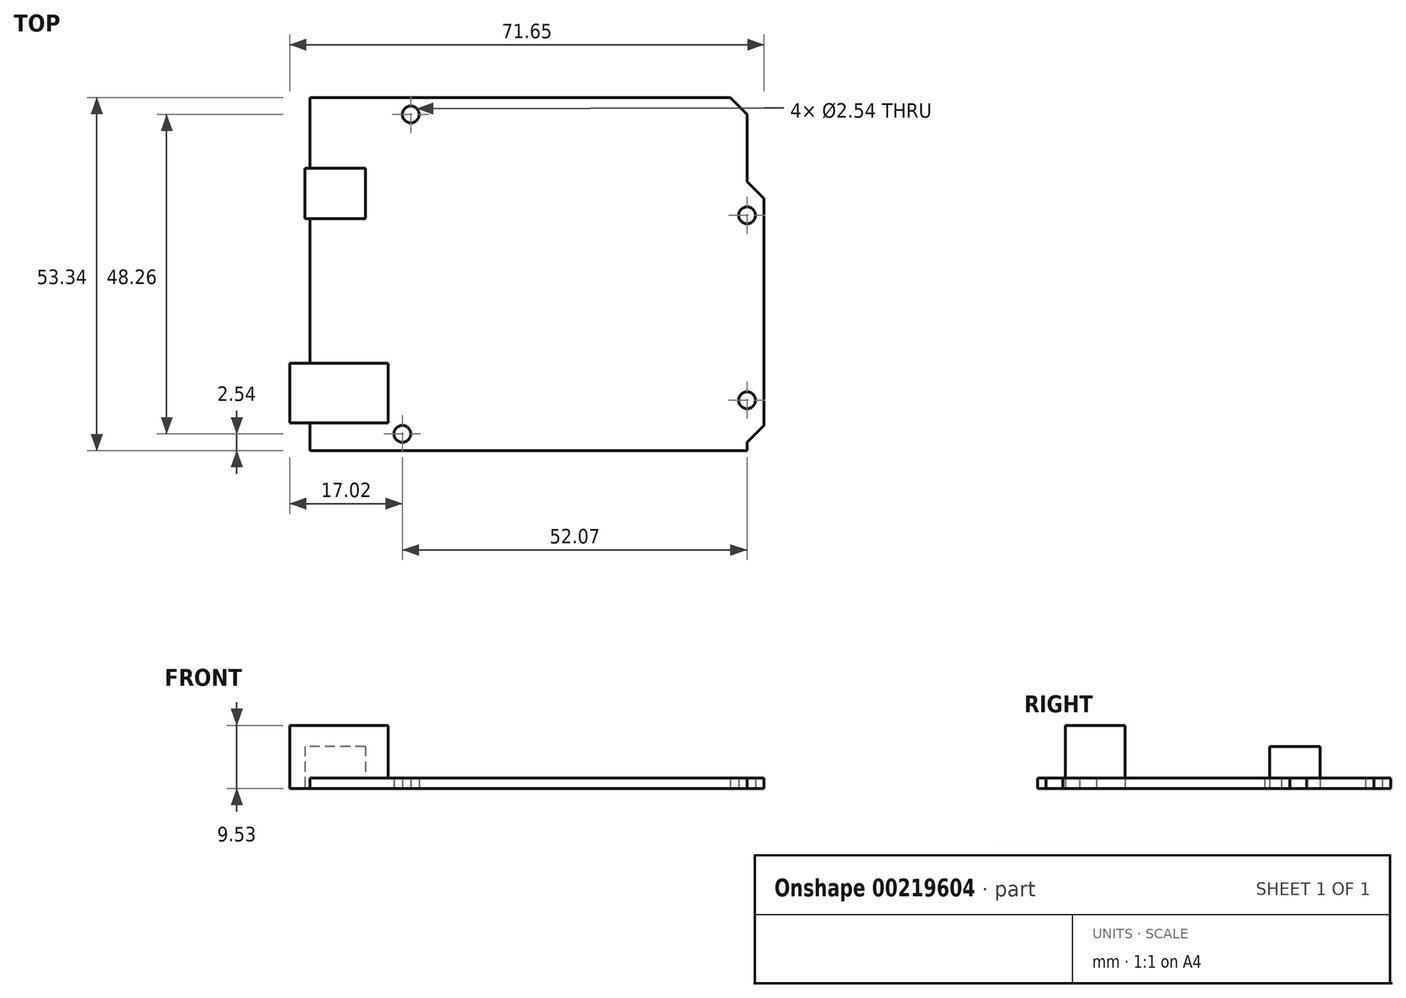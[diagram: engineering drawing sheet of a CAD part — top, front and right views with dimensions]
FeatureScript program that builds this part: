
annotation { "Feature Type Name" : "Feature", "Feature Type Description" : "" }
export const myFeature = defineFeature(function(context is Context, id is Id, definition is map)
    precondition{}
    {
        {
            var Q0;
            Q0=qCreatedBy(makeId("Top.planeOp"),FACE);
            var sketch = newSketch(context, id + "F0", { "sketchPlane" : qUnion([Q0])});
            skLineSegment(sketch, "E0.bottom", {"start": v(34.3, -26.67) * mm, "end": v(-34.3, -26.67) * mm});
            skLineSegment(sketch, "E0.right", {"start": v(-34.29, -26.67) * mm, "end": v(-34.3, 26.67) * mm});
            skPoint(sketch, "E0.middle", {"position": v(0, 0) * mm});
            skCircle(sketch, "E1", {"center": v(-19.05, 24.13) * mm, "radius": 1.27 * mm});
            skCircle(sketch, "E2", {"center": v(31.75, 8.9) * mm, "radius": 1.27 * mm});
            skCircle(sketch, "E3", {"center": v(31.75, -19.05) * mm, "radius": 1.27 * mm});
            skCircle(sketch, "E4", {"center": v(-20.32, -24.13) * mm, "radius": 1.27 * mm});
            skLineSegment(sketch, "E5", {"start": v(-34.3, 26.67) * mm, "end": v(-34.29, -26.67) * mm});
            skLineSegment(sketch, "E6", {"start": v(-34.3, -26.67) * mm, "end": v(34.3, -26.67) * mm});
            skLineSegment(sketch, "E7", {"start": v(31.8, -25.4) * mm, "end": v(31.8, -26.67) * mm});
            skLineSegment(sketch, "E8", {"start": v(31.8, -25.4) * mm, "end": v(34.31, -22.88) * mm});
            skLineSegment(sketch, "E9", {"start": v(34.31, 11.43) * mm, "end": v(31.77, 13.97) * mm});
            skLineSegment(sketch, "E10", {"start": v(34.31, -22.88) * mm, "end": v(34.31, 11.43) * mm});
            skLineSegment(sketch, "E11", {"start": v(-34.3, 26.67) * mm, "end": v(29.2, 26.67) * mm});
            skLineSegment(sketch, "E12", {"start": v(29.21, 26.67) * mm, "end": v(31.77, 24.13) * mm});
            skLineSegment(sketch, "E13", {"start": v(31.77, 24.13) * mm, "end": v(31.77, 13.97) * mm});
            skLineSegment(sketch, "E14.bottom", {"start": v(-22.48, -22.48) * mm, "end": v(-37.34, -22.48) * mm});
            skLineSegment(sketch, "E14.top", {"start": v(-22.48, -13.46) * mm, "end": v(-37.34, -13.46) * mm});
            skLineSegment(sketch, "E14.left", {"start": v(-22.48, -22.48) * mm, "end": v(-22.48, -13.46) * mm});
            skLineSegment(sketch, "E14.right", {"start": v(-37.34, -22.48) * mm, "end": v(-37.34, -13.46) * mm});
            skPoint(sketch, "E14.middle", {"position": v(-29.9, -17.97) * mm});
            skLineSegment(sketch, "E15.bottom", {"start": v(-25.9, 8.38) * mm, "end": v(-35.05, 8.38) * mm});
            skLineSegment(sketch, "E15.top", {"start": v(-25.9, 16) * mm, "end": v(-35.05, 16) * mm});
            skLineSegment(sketch, "E15.left", {"start": v(-25.9, 8.38) * mm, "end": v(-25.9, 16) * mm});
            skLineSegment(sketch, "E15.right", {"start": v(-35.05, 8.38) * mm, "end": v(-35.05, 16) * mm});
            skPoint(sketch, "E15.middle", {"position": v(-30.48, 12.2) * mm});
            skSolve(sketch);
        }
        {
            var Q0;
            Q0=makeQuery(id+"F0.imprint","IMPRINT",FACE,{"disambiguationData":[TD([[makeQuery(id+"F0.imprint","IMPRINT",EDGE,{"derivedFrom":sQuery(id+"F0.wireOp",EDGE,"E1")}),-1.0]])]});
            extrude(context, id + "F1", {"entities" : qUnion([Q0]), "depth" : 1.59 * mm});
        }
        {
            var Q0;
            {var subQ5=sQuery(id+"F0.wireOp",EDGE,"E15.left");Q0=makeQuery(id+"F0.imprint","IMPRINT",FACE,{"disambiguationData":[TD([[makeQuery(id+"F0.imprint","IMPRINT",EDGE,{"derivedFrom":subQ5}),1.0]])]});}
            var Q1;
            {var subQ5=sQuery(id+"F0.wireOp",EDGE,"E15.right");Q1=makeQuery(id+"F0.imprint","IMPRINT",FACE,{"disambiguationData":[TD([[makeQuery(id+"F0.imprint","IMPRINT",EDGE,{"derivedFrom":subQ5}),-1.0]])]});}
            extrude(context, id + "F2", {"entities" : qUnion([Q0, Q1]), "operationType" : NewBodyOperationType.ADD, "depth" : 6.35 * mm});
        }
        {
            var Q0;
            {var subQ5=sQuery(id+"F0.wireOp",EDGE,"E14.left");Q0=makeQuery(id+"F0.imprint","IMPRINT",FACE,{"disambiguationData":[TD([[makeQuery(id+"F0.imprint","IMPRINT",EDGE,{"derivedFrom":subQ5}),1.0]])]});}
            var Q1;
            {var subQ5=sQuery(id+"F0.wireOp",EDGE,"E14.right");Q1=makeQuery(id+"F0.imprint","IMPRINT",FACE,{"disambiguationData":[TD([[makeQuery(id+"F0.imprint","IMPRINT",EDGE,{"derivedFrom":subQ5}),-1.0]])]});}
            extrude(context, id + "F3", {"entities" : qUnion([Q0, Q1]), "operationType" : NewBodyOperationType.ADD, "depth" : 9.52 * mm});
        }
    });
